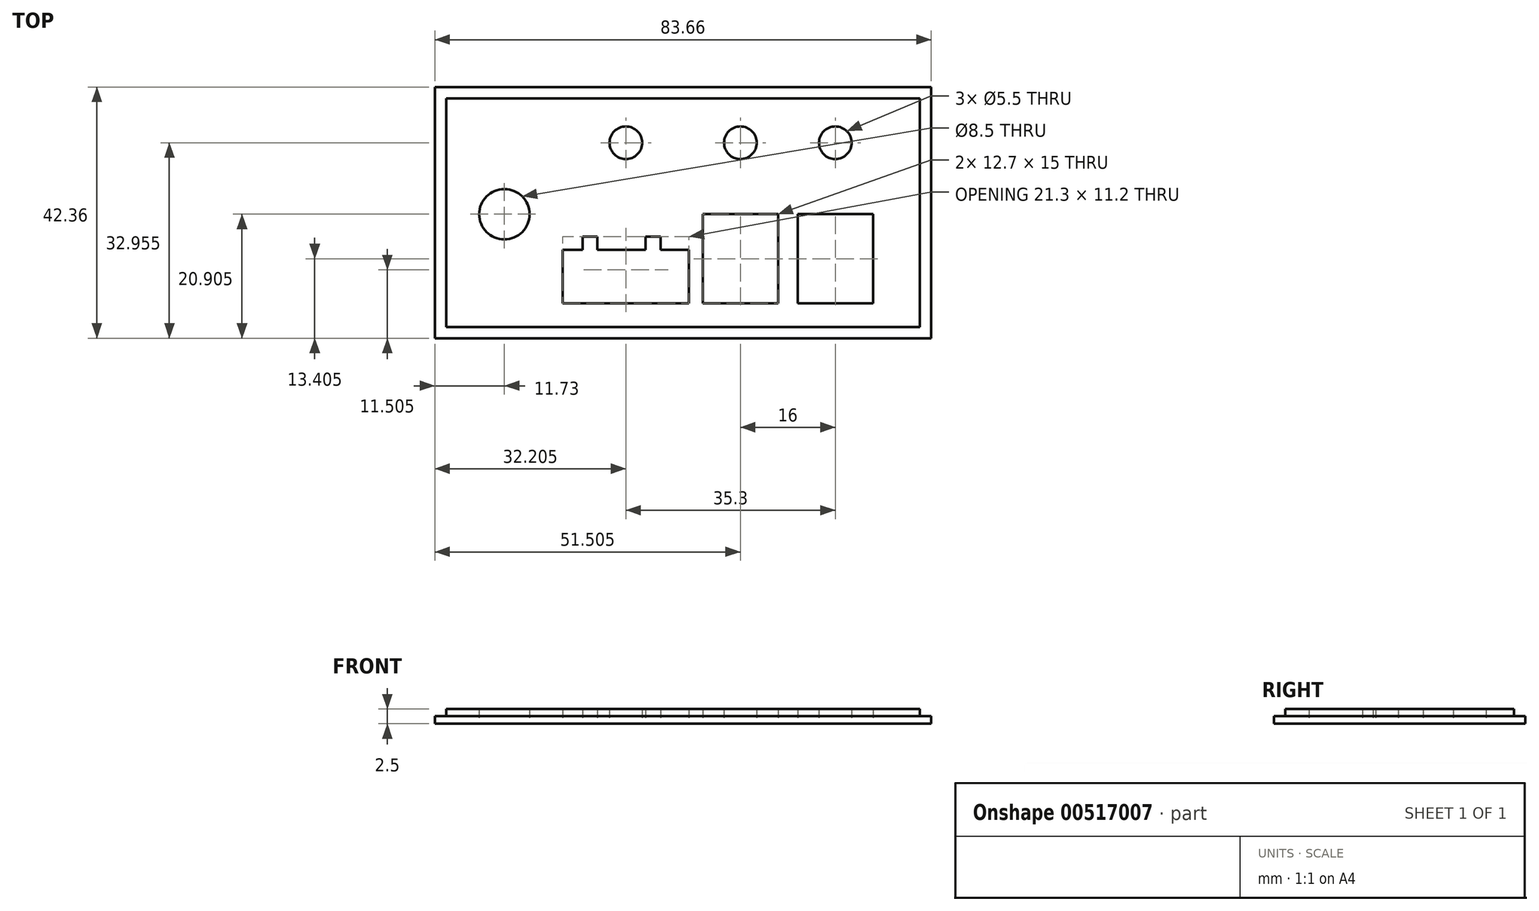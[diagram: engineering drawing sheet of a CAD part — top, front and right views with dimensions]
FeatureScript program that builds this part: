
annotation { "Feature Type Name" : "Feature", "Feature Type Description" : "" }
export const myFeature = defineFeature(function(context is Context, id is Id, definition is map)
    precondition{}
    {
        {
            var Q0;
            Q0=qCreatedBy(makeId("Top.planeOp"),FACE);
            var sketch = newSketch(context, id + "F0", { "sketchPlane" : qUnion([Q0])});
            skLineSegment(sketch, "E0.bottom", {"start": v(41.83, -21.18) * mm, "end": v(-41.82, -21.18) * mm});
            skLineSegment(sketch, "E0.top", {"start": v(41.83, 21.18) * mm, "end": v(-41.83, 21.18) * mm});
            skLineSegment(sketch, "E0.left", {"start": v(41.83, -21.17) * mm, "end": v(41.83, 21.18) * mm});
            skLineSegment(sketch, "E0.right", {"start": v(-41.82, -21.18) * mm, "end": v(-41.82, 21.17) * mm});
            skPoint(sketch, "E0.middle", {"position": v(0, 0) * mm});
            skLineSegment(sketch, "E1.bottom", {"start": v(39.93, -19.28) * mm, "end": v(-39.93, -19.28) * mm});
            skLineSegment(sketch, "E1.top", {"start": v(39.93, 19.28) * mm, "end": v(-39.93, 19.28) * mm});
            skLineSegment(sketch, "E1.left", {"start": v(39.92, -19.28) * mm, "end": v(39.92, 19.28) * mm});
            skLineSegment(sketch, "E1.right", {"start": v(-39.92, -19.28) * mm, "end": v(-39.92, 19.28) * mm});
            skLineSegment(sketch, "E2", {"start": v(-39.92, -15.28) * mm, "end": v(39.92, -15.27) * mm, "construction": true});
            skLineSegment(sketch, "E3.bottom", {"start": v(32.02, -15.27) * mm, "end": v(19.32, -15.27) * mm});
            skLineSegment(sketch, "E3.top", {"start": v(32.02, -0.27) * mm, "end": v(19.32, -0.27) * mm});
            skLineSegment(sketch, "E3.left", {"start": v(32.02, -15.27) * mm, "end": v(32.02, -0.27) * mm});
            skLineSegment(sketch, "E3.right", {"start": v(19.32, -15.28) * mm, "end": v(19.32, -0.27) * mm});
            skLineSegment(sketch, "E4.bottom", {"start": v(16.02, -15.28) * mm, "end": v(3.32, -15.28) * mm});
            skLineSegment(sketch, "E4.top", {"start": v(16.02, -0.28) * mm, "end": v(3.32, -0.28) * mm});
            skLineSegment(sketch, "E4.left", {"start": v(16.02, -15.28) * mm, "end": v(16.02, -0.28) * mm});
            skLineSegment(sketch, "E4.right", {"start": v(3.32, -15.28) * mm, "end": v(3.33, -0.28) * mm});
            skLineSegment(sketch, "E5.bottom", {"start": v(1.02, -15.28) * mm, "end": v(-20.28, -15.28) * mm});
            skLineSegment(sketch, "E5.top", {"start": v(1.02, -6.28) * mm, "end": v(-3.78, -6.28) * mm});
            skLineSegment(sketch, "E5.left", {"start": v(1.02, -15.28) * mm, "end": v(1.02, -6.28) * mm});
            skLineSegment(sketch, "E5.right", {"start": v(-20.28, -15.28) * mm, "end": v(-20.28, -6.28) * mm});
            skLineSegment(sketch, "E6", {"start": v(39.92, -0.27) * mm, "end": v(-39.92, -0.28) * mm, "construction": true});
            skLineSegment(sketch, "E7", {"start": v(-20.28, -10.78) * mm, "end": v(-39.92, -10.78) * mm, "construction": true});
            skLineSegment(sketch, "E8", {"start": v(39.92, 11.77) * mm, "end": v(-39.92, 11.78) * mm, "construction": true});
            skLineSegment(sketch, "E9", {"start": v(-30.1, -10.78) * mm, "end": v(-30.1, 19.28) * mm, "construction": true});
            skCircle(sketch, "E10", {"center": v(-30.1, -0.28) * mm, "radius": 4.25 * mm});
            skLineSegment(sketch, "E11", {"start": v(9.67, -0.28) * mm, "end": v(9.67, 19.28) * mm, "construction": true});
            skLineSegment(sketch, "E12", {"start": v(25.67, -0.27) * mm, "end": v(25.67, 19.27) * mm, "construction": true});
            skLineSegment(sketch, "E13", {"start": v(-9.63, -6.28) * mm, "end": v(-9.63, 19.28) * mm, "construction": true});
            skCircle(sketch, "E14", {"center": v(25.67, 11.77) * mm, "radius": 2.75 * mm});
            skCircle(sketch, "E15", {"center": v(9.67, 11.77) * mm, "radius": 2.75 * mm});
            skCircle(sketch, "E16", {"center": v(-9.63, 11.78) * mm, "radius": 2.75 * mm});
            skCircle(sketch, "E17", {"center": v(-30.1, 11.78) * mm, "radius": 2.75 * mm, "construction": true});
            skLineSegment(sketch, "E18.top", {"start": v(-3.78, -4.08) * mm, "end": v(-6.28, -4.08) * mm});
            skLineSegment(sketch, "E18.left", {"start": v(-3.78, -6.28) * mm, "end": v(-3.78, -4.08) * mm});
            skLineSegment(sketch, "E18.right", {"start": v(-6.28, -6.28) * mm, "end": v(-6.28, -4.08) * mm});
            skLineSegment(sketch, "E19.top", {"start": v(-14.43, -4.08) * mm, "end": v(-16.93, -4.08) * mm});
            skLineSegment(sketch, "E19.left", {"start": v(-14.43, -6.28) * mm, "end": v(-14.43, -4.08) * mm});
            skLineSegment(sketch, "E19.right", {"start": v(-16.93, -6.28) * mm, "end": v(-16.93, -4.08) * mm});
            skLineSegment(sketch, "E20.trimOffspring", {"start": v(-6.28, -6.28) * mm, "end": v(-14.43, -6.28) * mm});
            skLineSegment(sketch, "E21.trimOffspring", {"start": v(-16.93, -6.28) * mm, "end": v(-20.28, -6.28) * mm});
            skSolve(sketch);
        }
        {
            var Q0;
            Q0=makeQuery(id+"F0.imprint","IMPRINT",FACE,{"disambiguationData":[TD([[makeQuery(id+"F0.imprint","IMPRINT",EDGE,{"derivedFrom":sQuery(id+"F0.wireOp",EDGE,"E1.bottom")}),-1.0]])]});
            extrude(context, id + "F1", {"entities" : qUnion([Q0]), "depth" : 2.5 * mm, "offsetDistance" : 25 * mm});
        }
        {
            var Q0;
            Q0=makeQuery(id+"F0.imprint","IMPRINT",FACE,{"disambiguationData":[TD([[makeQuery(id+"F0.imprint","IMPRINT",EDGE,{"derivedFrom":sQuery(id+"F0.wireOp",EDGE,"E0.bottom")}),-1.0]])]});
            extrude(context, id + "F2", {"entities" : qUnion([Q0]), "operationType" : NewBodyOperationType.ADD, "depth" : 1.3 * mm, "offsetDistance" : 25 * mm});
        }
    });
